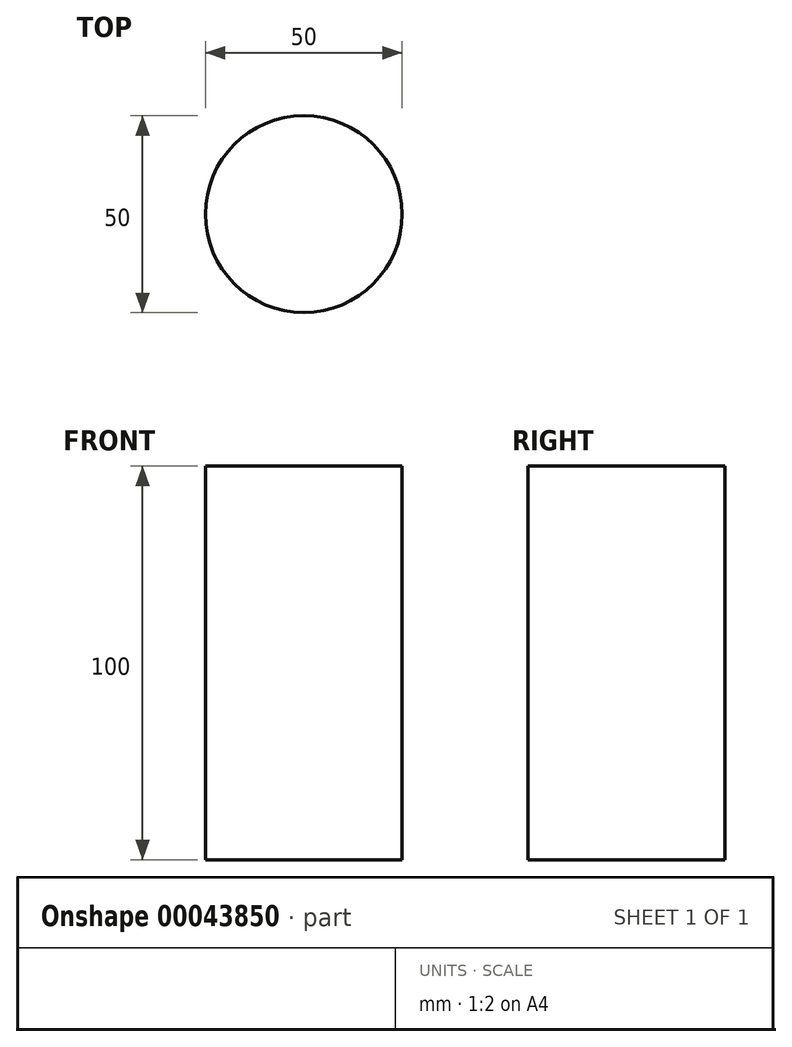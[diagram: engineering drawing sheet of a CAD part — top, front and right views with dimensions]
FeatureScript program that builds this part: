
annotation { "Feature Type Name" : "Feature", "Feature Type Description" : "" }
export const myFeature = defineFeature(function(context is Context, id is Id, definition is map)
    precondition{}
    {
        {
            var Q0;
            Q0=qCreatedBy(makeId("Top.planeOp"),FACE);
            var sketch = newSketch(context, id + "F0", { "sketchPlane" : qUnion([Q0])});
            skCircle(sketch, "E0", {"center": v(0, 0) * mm, "radius": 25 * mm});
            skSolve(sketch);
        }
        {
            var Q0;
            Q0=makeQuery(id+"F0.imprint","IMPRINT",FACE,{"disambiguationData":[TD([[makeQuery(id+"F0.imprint","IMPRINT",EDGE,{"derivedFrom":sQuery(id+"F0.wireOp",EDGE,"E0")}),1.0]])]});
            extrude(context, id + "F1", {"entities" : qUnion([Q0]), "depth" : 100 * mm});
        }
    });
